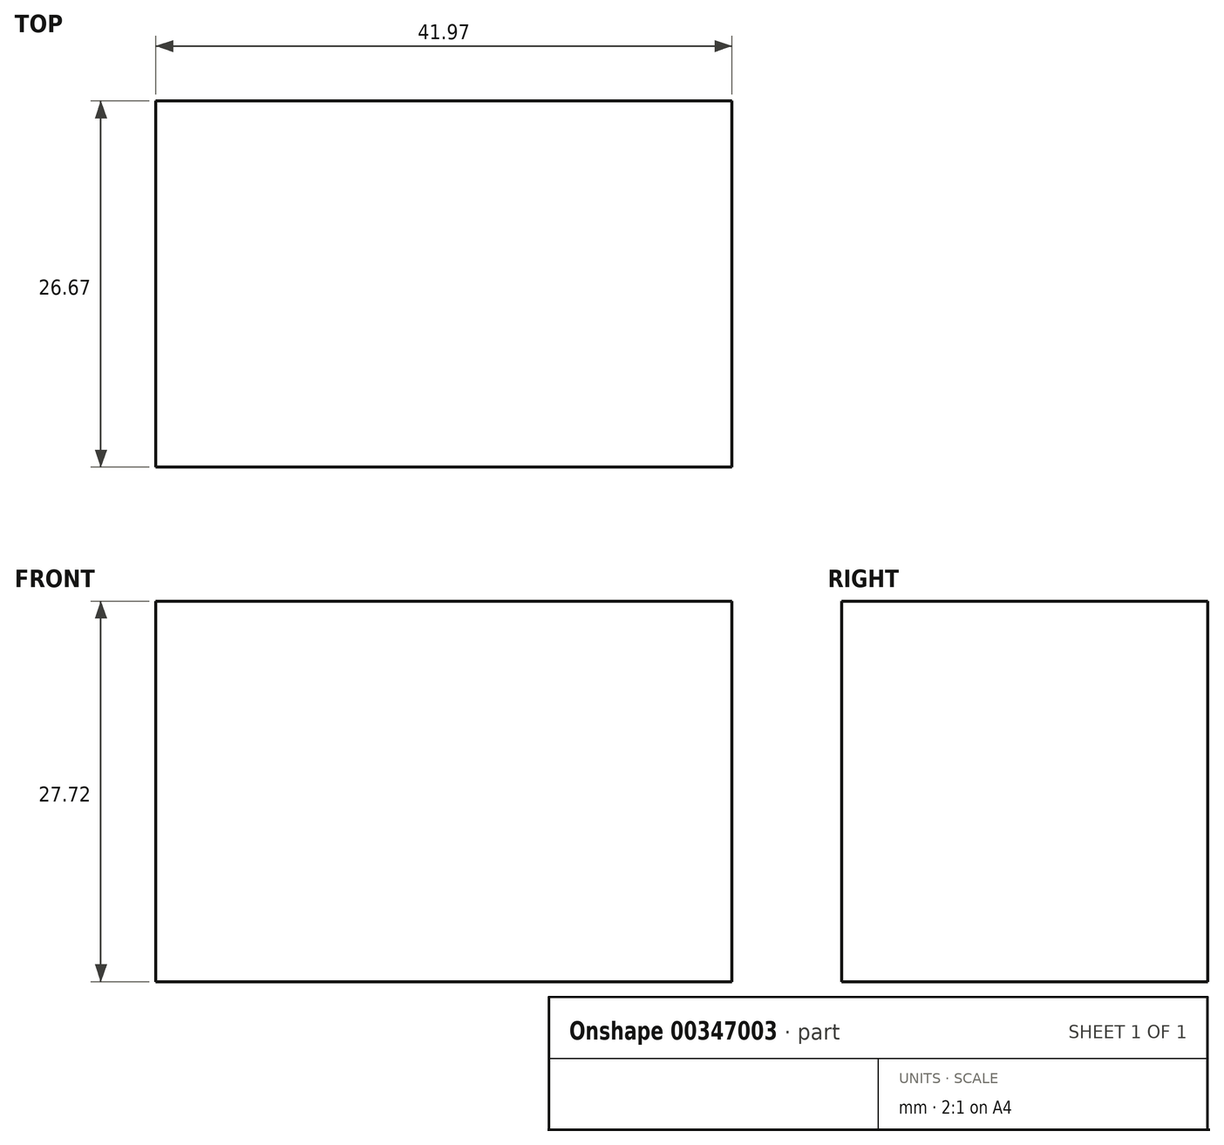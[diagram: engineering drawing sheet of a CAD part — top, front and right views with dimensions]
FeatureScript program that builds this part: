
annotation { "Feature Type Name" : "Feature", "Feature Type Description" : "" }
export const myFeature = defineFeature(function(context is Context, id is Id, definition is map)
    precondition{}
    {
        {
            var Q0;
            Q0=qCreatedBy(makeId("Front.planeOp"),FACE);
            var sketch = newSketch(context, id + "F0", { "sketchPlane" : qUnion([Q0])});
            skLineSegment(sketch, "E0.bottom", {"start": v(0, 0) * mm, "end": v(41.97, 0) * mm});
            skLineSegment(sketch, "E0.top", {"start": v(0, 27.72) * mm, "end": v(41.97, 27.72) * mm});
            skLineSegment(sketch, "E0.left", {"start": v(0, 0) * mm, "end": v(0, 27.72) * mm});
            skLineSegment(sketch, "E0.right", {"start": v(41.97, 0) * mm, "end": v(41.97, 27.72) * mm});
            skSolve(sketch);
        }
        {
            var Q0;
            Q0 = qSketchRegion(id + "F0", true);
            extrude(context, id + "F1", {"entities" : qUnion([Q0]), "oppositeDirection" : true, "depth" : 26.67 * mm});
        }
    });
